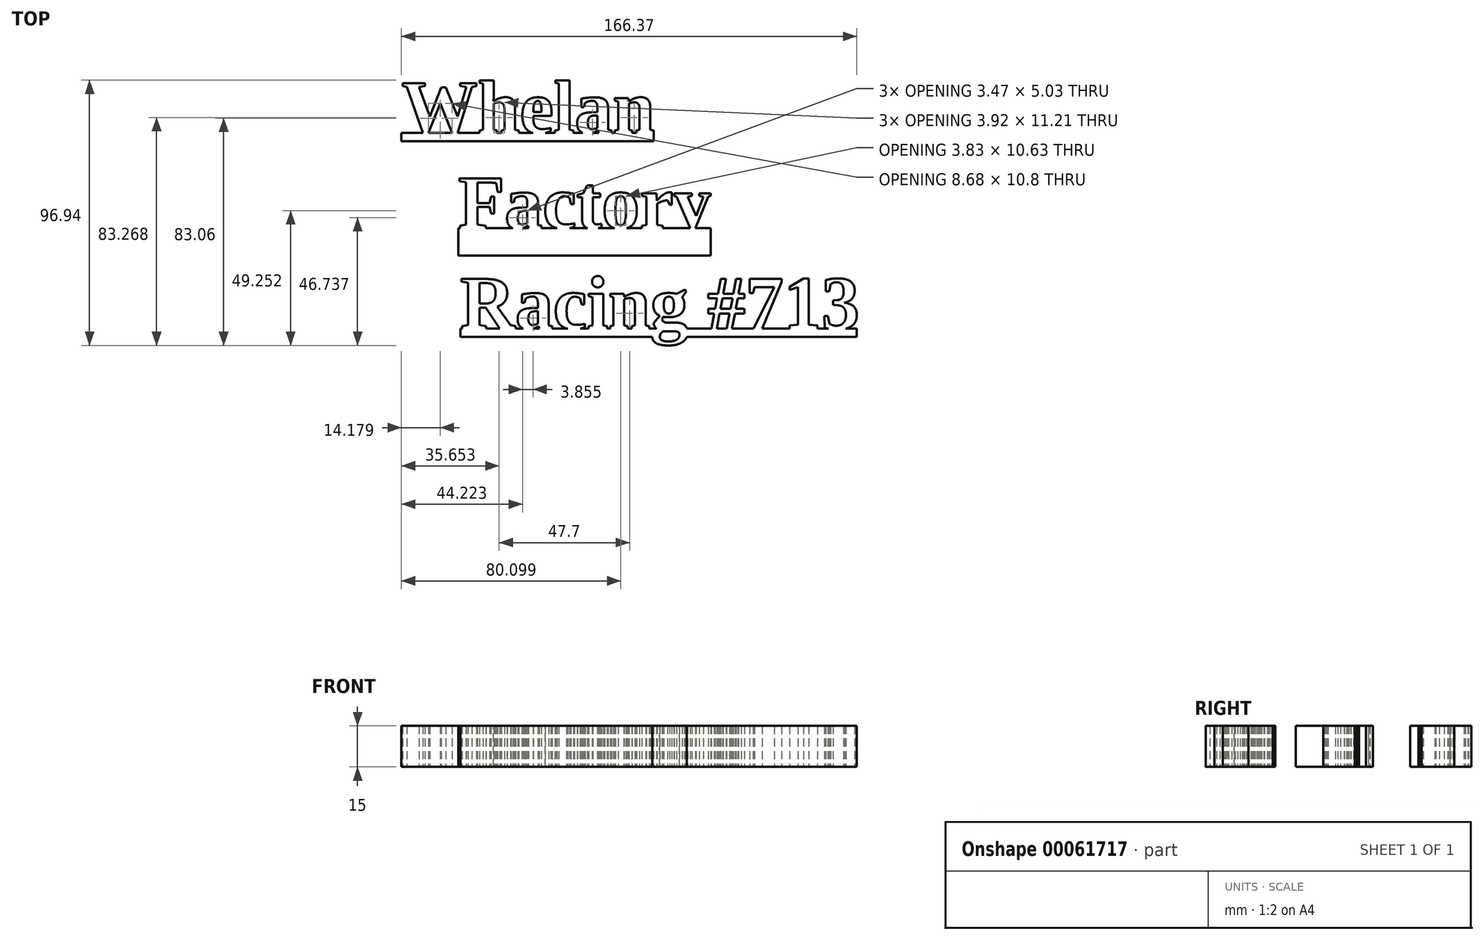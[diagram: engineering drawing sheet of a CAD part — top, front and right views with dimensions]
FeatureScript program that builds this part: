
annotation { "Feature Type Name" : "Feature", "Feature Type Description" : "" }
export const myFeature = defineFeature(function(context is Context, id is Id, definition is map)
    precondition{}
    {
        {
            var Q0;
            Q0=qCreatedBy(makeId("Top.planeOp"),FACE);
            var sketch = newSketch(context, id + "F0", { "sketchPlane" : qUnion([Q0])});
            skText(sketch, "E0", { "text": "Whelan", "fontName": "Tinos-Bold.ttf"});
            skLineSegment(sketch, "E1.bottom", {"start": v(-58.15, 34.81) * mm, "end": v(34.04, 34.81) * mm});
            skLineSegment(sketch, "E1.top", {"start": v(-58.15, 31.81) * mm, "end": v(34.04, 31.81) * mm});
            skLineSegment(sketch, "E1.left", {"start": v(-58.15, 34.81) * mm, "end": v(-58.15, 31.81) * mm});
            skLineSegment(sketch, "E1.right", {"start": v(34.04, 34.81) * mm, "end": v(34.04, 31.81) * mm});
            skText(sketch, "E2", { "text": "Factory", "fontName": "Tinos-Bold.ttf"});
            skLineSegment(sketch, "E3.bottom", {"start": v(-37.43, 0) * mm, "end": v(54.85, 0) * mm});
            skLineSegment(sketch, "E3.top", {"start": v(-37.43, -10) * mm, "end": v(54.85, -10) * mm});
            skLineSegment(sketch, "E3.left", {"start": v(-37.43, 0) * mm, "end": v(-37.43, -10) * mm});
            skLineSegment(sketch, "E3.right", {"start": v(54.85, 0) * mm, "end": v(54.85, -10) * mm});
            skText(sketch, "E4", { "text": "Racing #713", "fontName": "Tinos-Bold.ttf"});
            skLineSegment(sketch, "E5.bottom", {"start": v(-36.67, -36.72) * mm, "end": v(108.22, -36.72) * mm});
            skLineSegment(sketch, "E5.top", {"start": v(-36.67, -39.72) * mm, "end": v(108.22, -39.72) * mm});
            skLineSegment(sketch, "E5.left", {"start": v(-36.67, -36.72) * mm, "end": v(-36.67, -39.72) * mm});
            skLineSegment(sketch, "E5.right", {"start": v(108.22, -36.72) * mm, "end": v(108.22, -39.72) * mm});
            const initialGuessF0  = {"E0": [-0.05815, 0.03481, 1, 0, 0.02], "E2": [-0.03743, 0, 1, 0, 0.02], "E4": [-0.03667, -0.03672, 1, 0, 0.02]};
            skSetInitialGuess(sketch, initialGuessF0);
            skSolve(sketch);
        }
        {
            var Q0;
            Q0 = qSketchRegion(id + "F0", true);
            extrude(context, id + "F1", {"entities" : qUnion([Q0]), "depth" : 15 * mm});
        }
    });
